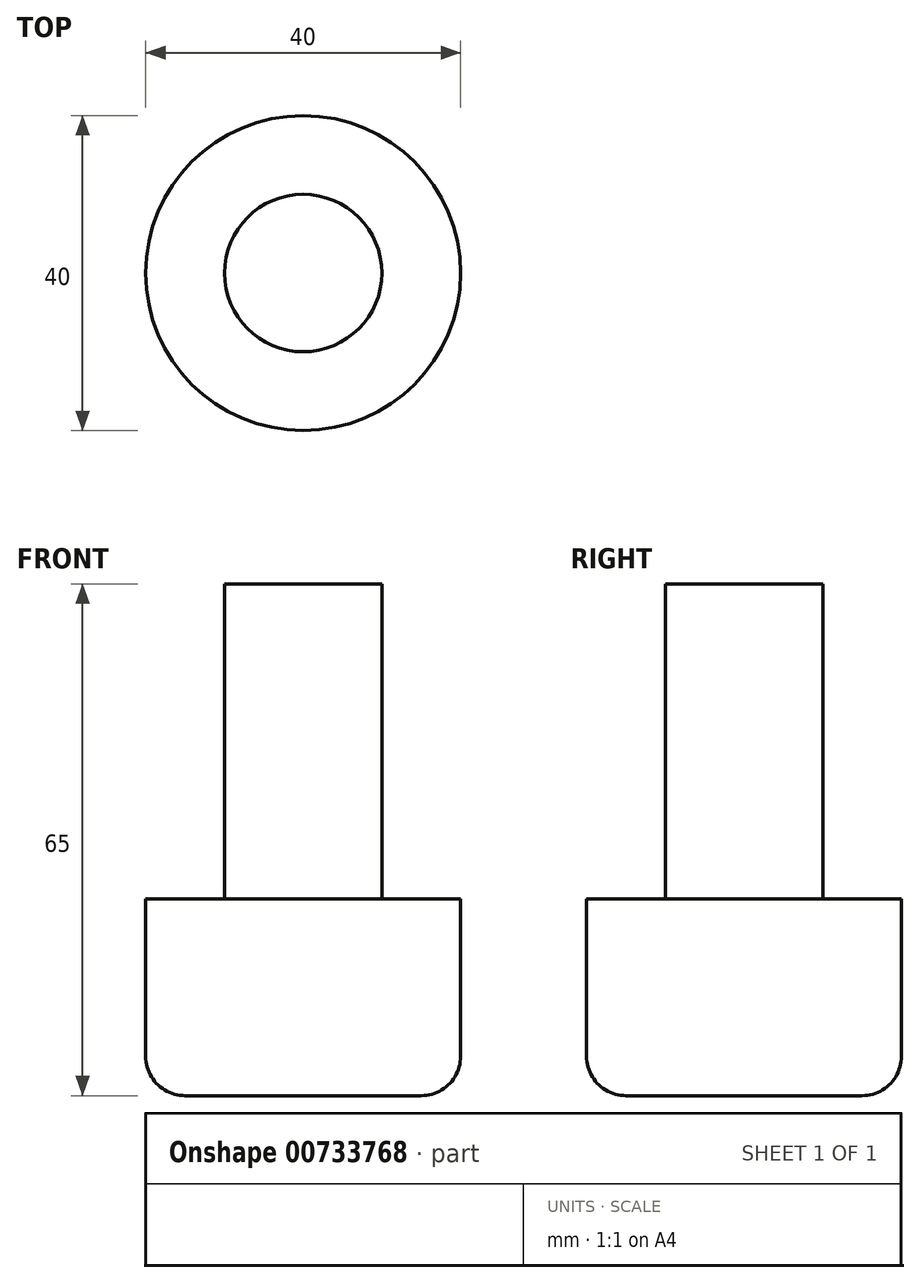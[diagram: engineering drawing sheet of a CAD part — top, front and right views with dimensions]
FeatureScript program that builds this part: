
annotation { "Feature Type Name" : "Feature", "Feature Type Description" : "" }
export const myFeature = defineFeature(function(context is Context, id is Id, definition is map)
    precondition{}
    {
        {
            var Q0;
            Q0=qCreatedBy(makeId("Top.planeOp"),FACE);
            var sketch = newSketch(context, id + "F0", { "sketchPlane" : qUnion([Q0])});
            skCircle(sketch, "E0", {"center": v(0, 0) * mm, "radius": 20 * mm});
            skSolve(sketch);
        }
        {
            var Q0;
            Q0=makeQuery(id+"F0.imprint","IMPRINT",FACE,{"disambiguationData":[TD([[makeQuery(id+"F0.imprint","IMPRINT",EDGE,{"derivedFrom":sQuery(id+"F0.wireOp",EDGE,"E0")}),1.0]])]});
            extrude(context, id + "F1", {"entities" : qUnion([Q0]), "oppositeDirection" : true, "depth" : 25 * mm, "offsetDistance" : 25 * mm});
        }
        {
            var Q0;
            Q0=qCreatedBy(makeId("Top.planeOp"),FACE);
            var sketch = newSketch(context, id + "F2", { "sketchPlane" : qUnion([Q0])});
            skCircle(sketch, "E1", {"center": v(0, 0) * mm, "radius": 10 * mm});
            skSolve(sketch);
        }
        {
            var Q0;
            Q0=qSketchRegion(id+"F2",true);
            extrude(context, id + "F3", {"entities" : qUnion([Q0]), "operationType" : NewBodyOperationType.ADD, "depth" : 40 * mm, "offsetDistance" : 25 * mm});
        }
        {
            var Q0;
            Q0=makeQuery(id+"F1.opExtrude","CAP_EDGE",EDGE,{"disambiguationData":[OSD([sQuery(id+"F0.wireOp",EDGE,"E0")])],"isStart":false});
            fillet(context, id + "F4", {"entities" : qUnion([Q0]), "radius" : 5 * mm, "tangentPropagation" : true, "allowEdgeOverflow" : false});
        }
    });
